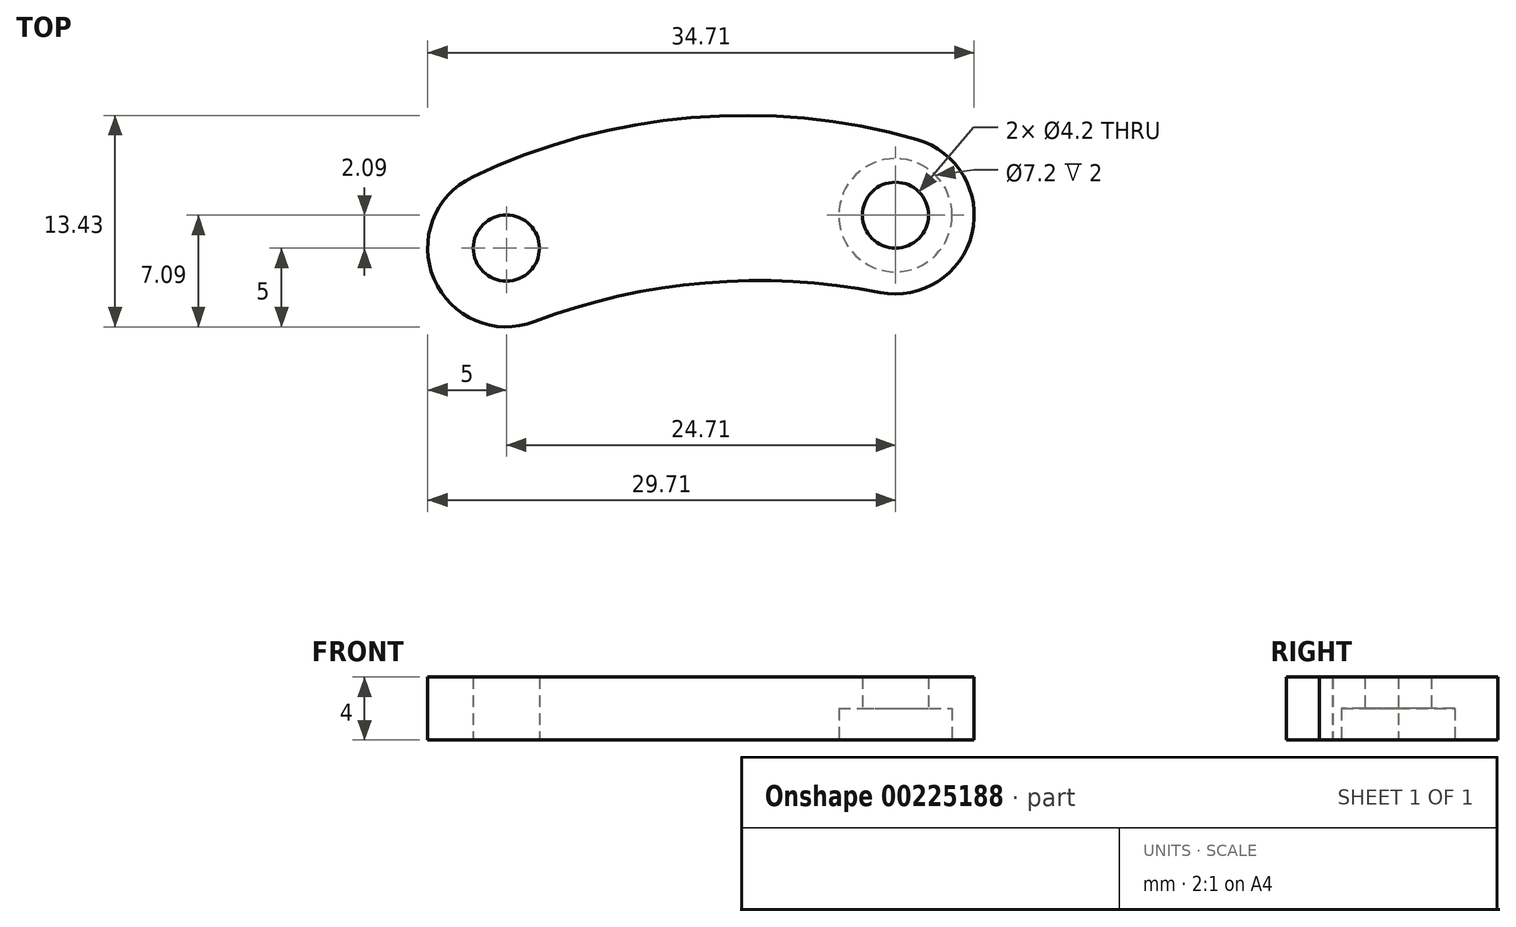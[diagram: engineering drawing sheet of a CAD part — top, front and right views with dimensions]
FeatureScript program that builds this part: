
annotation { "Feature Type Name" : "Feature", "Feature Type Description" : "" }
export const myFeature = defineFeature(function(context is Context, id is Id, definition is map)
    precondition{}
    {
        {
            var Q0;
            Q0=qCreatedBy(makeId("Top.planeOp"),FACE);
            var sketch = newSketch(context, id + "F0", { "sketchPlane" : qUnion([Q0])});
            skCircle(sketch, "E0", {"center": v(0, 0) * mm, "radius": 2.1 * mm});
            skCircle(sketch, "E1", {"center": v(0, 0) * mm, "radius": 5 * mm});
            skCircle(sketch, "E2", {"center": v(24.71, 2.1) * mm, "radius": 2.1 * mm});
            skCircle(sketch, "E3", {"center": v(24.71, 2.1) * mm, "radius": 5 * mm});
            skArc(sketch, "E4.trimOffspring", {"start": v(23.74, -2.82) * mm, "mid": v(12.63, -2.2) * mm, "end": v(1.78, -4.67) * mm});
            skArc(sketch, "E5.trimOffspring", {"start": v(26.08, 6.9) * mm, "mid": v(11.74, 8.29) * mm, "end": v(-2.16, 4.5) * mm});
            skSolve(sketch);
        }
        {
            var Q0;
            Q0 = qSketchRegion(id + "F0", true);
            extrude(context, id + "F1", {"entities" : qUnion([Q0]), "depth" : 4 * mm});
        }
        {
            var Q0;
            Q0=makeQuery(id+"F1.opExtrude","CAP_FACE",FACE,{"disambiguationData":[OSD([sQuery(id+"F0.wireOp",EDGE,"E0"),sQuery(id+"F0.wireOp",EDGE,"E1"),sQuery(id+"F0.wireOp",EDGE,"E2"),sQuery(id+"F0.wireOp",EDGE,"E3"),sQuery(id+"F0.wireOp",EDGE,"E4.trimOffspring"),sQuery(id+"F0.wireOp",EDGE,"E5.trimOffspring")])],"isStart":true});
            var sketch = newSketch(context, id + "F2", { "sketchPlane" : qUnion([Q0])});
            skCircle(sketch, "E6", {"center": v(24.71, -2.1) * mm, "radius": 3.6 * mm});
            skSolve(sketch);
        }
        {
            var Q0;
            Q0 = qSketchRegion(id + "F2", true);
            extrude(context, id + "F3", {"entities" : qUnion([Q0]), "operationType" : NewBodyOperationType.REMOVE, "oppositeDirection" : true, "depth" : 2 * mm});
        }
    });
